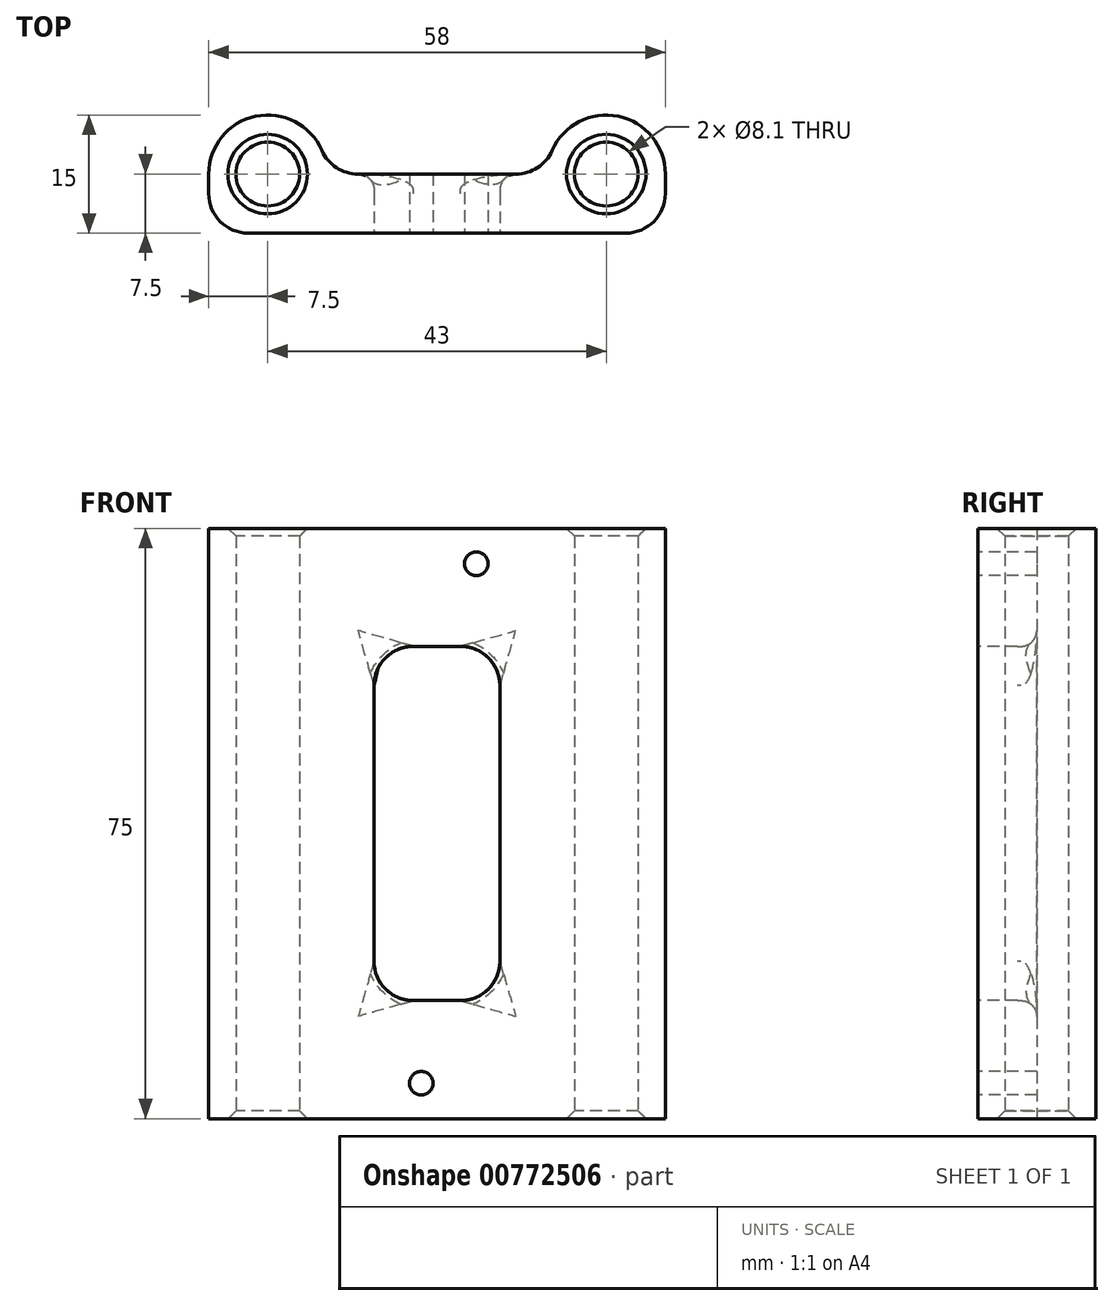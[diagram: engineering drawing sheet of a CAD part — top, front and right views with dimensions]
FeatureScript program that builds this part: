
annotation { "Feature Type Name" : "Feature", "Feature Type Description" : "" }
export const myFeature = defineFeature(function(context is Context, id is Id, definition is map)
    precondition{}
    {
        {
            var Q0;
            Q0=qCreatedBy(makeId("Top.planeOp"),FACE);
            var sketch = newSketch(context, id + "F0", { "sketchPlane" : qUnion([Q0])});
            skLineSegment(sketch, "E0.bottom", {"start": v(29, -7.5) * mm, "end": v(-29, -7.5) * mm});
            skLineSegment(sketch, "E0.left", {"start": v(29, -7.5) * mm, "end": v(29, 0) * mm});
            skLineSegment(sketch, "E0.right", {"start": v(-29, -7.5) * mm, "end": v(-29, 0) * mm});
            skPoint(sketch, "E0.middle", {"position": v(0, 0) * mm});
            skCircle(sketch, "E1", {"center": v(-21.5, 0) * mm, "radius": 4.05 * mm});
            skCircle(sketch, "E2", {"center": v(21.5, 0) * mm, "radius": 4.05 * mm});
            skLineSegment(sketch, "E3", {"start": v(0, 0) * mm, "end": v(-14, 0) * mm});
            skLineSegment(sketch, "E4", {"start": v(0, 0) * mm, "end": v(14, 0) * mm});
            skArc(sketch, "E5", {"start": v(-14, 0) * mm, "mid": v(-21.5, 7.5) * mm, "end": v(-29, 0) * mm});
            skArc(sketch, "E6", {"start": v(29, 0) * mm, "mid": v(21.5, 7.5) * mm, "end": v(14, 0) * mm});
            skPoint(sketch, "E7.orphan", {"position": v(29, 7.5) * mm});
            skPoint(sketch, "E8.orphan", {"position": v(-29, 7.5) * mm});
            skSolve(sketch);
        }
        {
            var Q0;
            Q0=makeQuery(id+"F0.imprint","IMPRINT",FACE,{"disambiguationData":[TD([[makeQuery(id+"F0.imprint","IMPRINT",EDGE,{"derivedFrom":sQuery(id+"F0.wireOp",EDGE,"E0.bottom")}),-1.0]])]});
            extrude(context, id + "F1", {"entities" : qUnion([Q0]), "depth" : 75 * mm, "offsetDistance" : 25 * mm});
        }
        {
            var Q0;
            Q0=makeQuery(id+"F1.opExtrude","SWEPT_FACE",FACE,{"disambiguationData":[OSD([sQuery(id+"F0.wireOp",EDGE,"E0.bottom")])]});
            var sketch = newSketch(context, id + "F2", { "sketchPlane" : qUnion([Q0])});
            skCircle(sketch, "E9", {"center": v(-2, 4.5) * mm, "radius": 1.5 * mm});
            skCircle(sketch, "E10", {"center": v(5, 70.5) * mm, "radius": 1.5 * mm});
            skLineSegment(sketch, "E11.bottom", {"start": v(8, 60) * mm, "end": v(-8, 60) * mm});
            skLineSegment(sketch, "E11.top", {"start": v(8, 15) * mm, "end": v(-8, 15) * mm});
            skLineSegment(sketch, "E11.left", {"start": v(8, 60) * mm, "end": v(8, 15) * mm});
            skLineSegment(sketch, "E11.right", {"start": v(-8, 60) * mm, "end": v(-8, 15) * mm});
            skPoint(sketch, "E11.middle", {"position": v(0, 37.5) * mm});
            skPoint(sketch, "E11.middle.positionSnap0", {"position": v(-29, 37.5) * mm});
            skPoint(sketch, "E11.centerSnap0", {"position": v(-29, 37.5) * mm});
            skSolve(sketch);
        }
        {
            var Q0;
            Q0=makeQuery(id+"F2.imprint","IMPRINT",FACE,{"disambiguationData":[TD([[makeQuery(id+"F2.imprint","IMPRINT",EDGE,{"derivedFrom":sQuery(id+"F2.wireOp",EDGE,"E10")}),1.0]])]});
            var Q1;
            Q1=makeQuery(id+"F2.imprint","IMPRINT",FACE,{"disambiguationData":[TD([[makeQuery(id+"F2.imprint","IMPRINT",EDGE,{"derivedFrom":sQuery(id+"F2.wireOp",EDGE,"E9")}),1.0]])]});
            var Q2;
            Q2=makeQuery(id+"F2.imprint","IMPRINT",FACE,{"disambiguationData":[TD([[makeQuery(id+"F2.imprint","IMPRINT",EDGE,{"derivedFrom":sQuery(id+"F2.wireOp",EDGE,"E11.bottom")}),1.0]])]});
            extrude(context, id + "F3", {"entities" : qUnion([Q0, Q1, Q2]), "operationType" : NewBodyOperationType.REMOVE, "endBound" : BoundingType.THROUGH_ALL, "oppositeDirection" : true, "depth" : 25 * mm, "offsetDistance" : 25 * mm});
        }
        {
            var Q0;
            Q0=makeQuery(id+"F1.opExtrude","SWEPT_EDGE",EDGE,{"disambiguationData":[OSD([sQuery(id+"F0.wireOp",EDGE,"E3"),sQuery(id+"F0.wireOp",EDGE,"E5")])]});
            var Q1;
            Q1=makeQuery(id+"F1.opExtrude","SWEPT_EDGE",EDGE,{"disambiguationData":[OSD([sQuery(id+"F0.wireOp",EDGE,"E4"),sQuery(id+"F0.wireOp",EDGE,"E6")])]});
            var Q2;
            Q2=makeQuery(id+"F1.opExtrude","SWEPT_EDGE",EDGE,{"disambiguationData":[OSD([sQuery(id+"F0.wireOp",EDGE,"E0.bottom"),sQuery(id+"F0.wireOp",EDGE,"E0.right")])]});
            var Q3;
            Q3=makeQuery(id+"F1.opExtrude","SWEPT_EDGE",EDGE,{"disambiguationData":[OSD([sQuery(id+"F0.wireOp",EDGE,"E0.bottom"),sQuery(id+"F0.wireOp",EDGE,"E0.left")])]});
            fillet(context, id + "F4", {"entities" : qUnion([Q0, Q1, Q2, Q3]), "radius" : 5 * mm, "tangentPropagation" : true, "allowEdgeOverflow" : false});
        }
        {
            var Q0;
            Q0=makeQuery(id+"F1.opExtrude","CAP_EDGE",EDGE,{"disambiguationData":[OSD([sQuery(id+"F0.wireOp",EDGE,"E1")])],"isStart":false});
            var Q1;
            Q1=makeQuery(id+"F1.opExtrude","CAP_EDGE",EDGE,{"disambiguationData":[OSD([sQuery(id+"F0.wireOp",EDGE,"E2")])],"isStart":false});
            var Q2;
            Q2=makeQuery(id+"F1.opExtrude","CAP_EDGE",EDGE,{"disambiguationData":[OSD([sQuery(id+"F0.wireOp",EDGE,"E1")])],"isStart":true});
            var Q3;
            Q3=makeQuery(id+"F1.opExtrude","CAP_EDGE",EDGE,{"disambiguationData":[OSD([sQuery(id+"F0.wireOp",EDGE,"E2")])],"isStart":true});
            chamfer(context, id + "F5", {"entities" : qUnion([Q0, Q1, Q2, Q3]), "width" : 1 * mm, "tangentPropagation" : true});
        }
        {
            var Q0;
            Q0=makeQuery(id+"F3.boolean.opBoolean","INTERSECT",EDGE,{"derivedFrom":[makeQuery(id+"F1.opExtrude","SWEPT_FACE",FACE,{"disambiguationData":[OSD([sQuery(id+"F0.wireOp",EDGE,"E3"),sQuery(id+"F0.wireOp",EDGE,"E4")])]}),makeQuery(id+"F3.opExtrude","SWEPT_FACE",FACE,{"disambiguationData":[OSD([sQuery(id+"F2.wireOp",EDGE,"E11.top")])]})]});
            var Q1;
            Q1=makeQuery(id+"F3.boolean.opBoolean","INTERSECT",EDGE,{"derivedFrom":[makeQuery(id+"F1.opExtrude","SWEPT_FACE",FACE,{"disambiguationData":[OSD([sQuery(id+"F0.wireOp",EDGE,"E3"),sQuery(id+"F0.wireOp",EDGE,"E4")])]}),makeQuery(id+"F3.opExtrude","SWEPT_FACE",FACE,{"disambiguationData":[OSD([sQuery(id+"F2.wireOp",EDGE,"E11.right")])]})]});
            var Q2;
            Q2=makeQuery(id+"F3.boolean.opBoolean","INTERSECT",EDGE,{"derivedFrom":[makeQuery(id+"F1.opExtrude","SWEPT_FACE",FACE,{"disambiguationData":[OSD([sQuery(id+"F0.wireOp",EDGE,"E3"),sQuery(id+"F0.wireOp",EDGE,"E4")])]}),makeQuery(id+"F3.opExtrude","SWEPT_FACE",FACE,{"disambiguationData":[OSD([sQuery(id+"F2.wireOp",EDGE,"E11.bottom")])]})]});
            var Q3;
            Q3=makeQuery(id+"F3.boolean.opBoolean","INTERSECT",EDGE,{"derivedFrom":[makeQuery(id+"F1.opExtrude","SWEPT_FACE",FACE,{"disambiguationData":[OSD([sQuery(id+"F0.wireOp",EDGE,"E3"),sQuery(id+"F0.wireOp",EDGE,"E4")])]}),makeQuery(id+"F3.opExtrude","SWEPT_FACE",FACE,{"disambiguationData":[OSD([sQuery(id+"F2.wireOp",EDGE,"E11.left")])]})]});
            fillet(context, id + "F6", {"entities" : qUnion([Q0, Q1, Q2, Q3]), "radius" : 2 * mm, "tangentPropagation" : true, "allowEdgeOverflow" : false});
        }
        {
            var Q0;
            Q0=makeQuery(id+"F3.boolean.opBoolean","COPY",EDGE,{"derivedFrom":makeQuery(id+"F3.opExtrude","SWEPT_EDGE",EDGE,{"disambiguationData":[OSD([sQuery(id+"F2.wireOp",EDGE,"E11.top"),sQuery(id+"F2.wireOp",EDGE,"E11.left")])]})});
            var Q1;
            Q1=makeQuery(id+"F3.boolean.opBoolean","COPY",EDGE,{"derivedFrom":makeQuery(id+"F3.opExtrude","SWEPT_EDGE",EDGE,{"disambiguationData":[OSD([sQuery(id+"F2.wireOp",EDGE,"E11.top"),sQuery(id+"F2.wireOp",EDGE,"E11.right")])]})});
            var Q2;
            Q2=makeQuery(id+"F3.boolean.opBoolean","COPY",EDGE,{"derivedFrom":makeQuery(id+"F3.opExtrude","SWEPT_EDGE",EDGE,{"disambiguationData":[OSD([sQuery(id+"F2.wireOp",EDGE,"E11.bottom"),sQuery(id+"F2.wireOp",EDGE,"E11.left")])]})});
            var Q3;
            Q3=makeQuery(id+"F3.boolean.opBoolean","COPY",EDGE,{"derivedFrom":makeQuery(id+"F3.opExtrude","SWEPT_EDGE",EDGE,{"disambiguationData":[OSD([sQuery(id+"F2.wireOp",EDGE,"E11.bottom"),sQuery(id+"F2.wireOp",EDGE,"E11.right")])]})});
            fillet(context, id + "F7", {"entities" : qUnion([Q0, Q1, Q2, Q3]), "radius" : 5 * mm, "tangentPropagation" : true, "allowEdgeOverflow" : false});
        }
    });
